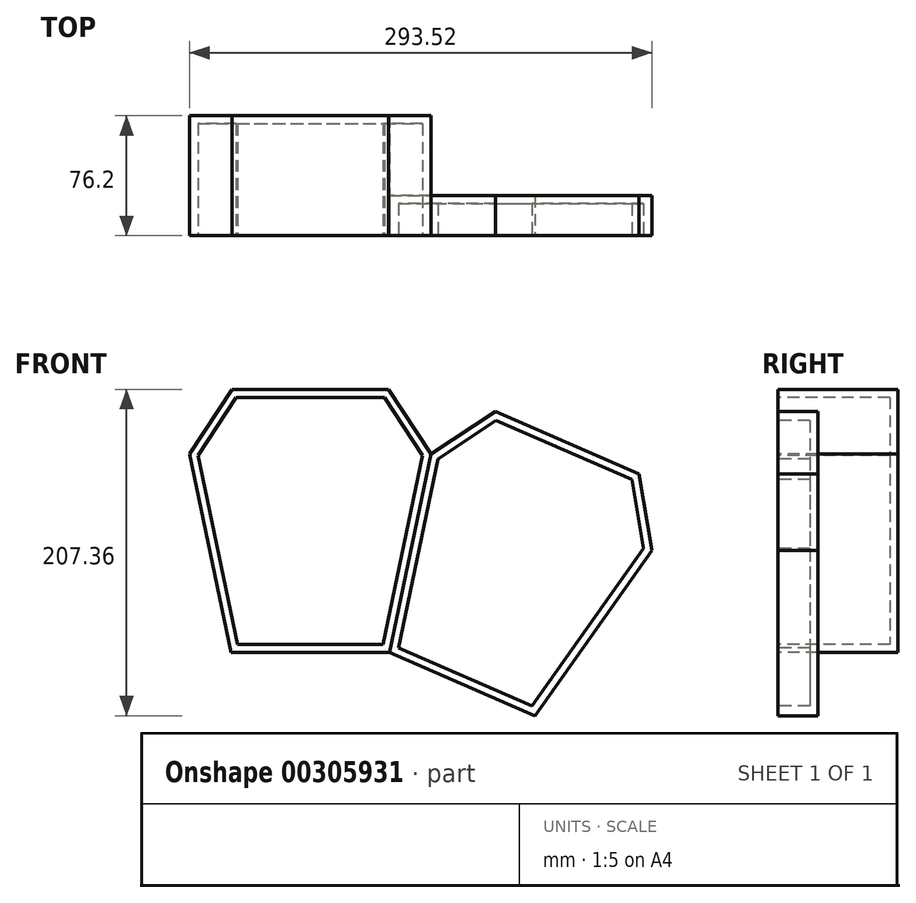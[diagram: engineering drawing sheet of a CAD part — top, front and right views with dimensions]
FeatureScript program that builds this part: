
annotation { "Feature Type Name" : "Feature", "Feature Type Description" : "" }
export const myFeature = defineFeature(function(context is Context, id is Id, definition is map)
    precondition{}
    {
        {
            var Q0;
            Q0=qCreatedBy(makeId("Front.planeOp"),FACE);
            var sketch = newSketch(context, id + "F0", { "sketchPlane" : qUnion([Q0])});
            skLineSegment(sketch, "E0", {"start": v(0, 0) * mm, "end": v(49.8, 0) * mm});
            skLineSegment(sketch, "E1", {"start": v(49.8, 0) * mm, "end": v(76.56, -41.16) * mm});
            skLineSegment(sketch, "E2", {"start": v(76.56, -41.16) * mm, "end": v(50.32, -167.2) * mm});
            skLineSegment(sketch, "E3", {"start": v(50.32, -167.2) * mm, "end": v(0, -167.2) * mm});
            skLineSegment(sketch, "E4.MirrorCS", {"start": v(0, 0) * mm, "end": v(-49.8, 0) * mm});
            skLineSegment(sketch, "E5.MirrorCS", {"start": v(-49.8, 0) * mm, "end": v(-76.56, -41.16) * mm});
            skLineSegment(sketch, "E6.MirrorCS", {"start": v(-76.56, -41.16) * mm, "end": v(-50.32, -167.2) * mm});
            skLineSegment(sketch, "E7.MirrorCS", {"start": v(-50.32, -167.2) * mm, "end": v(0, -167.2) * mm});
            skLineSegment(sketch, "E8.MirrorCS", {"start": v(117.52, -14.1) * mm, "end": v(76.56, -41.16) * mm});
            skLineSegment(sketch, "E9.MirrorCS", {"start": v(163.18, -33.96) * mm, "end": v(117.52, -14.1) * mm});
            skLineSegment(sketch, "E10.MirrorCS", {"start": v(163.18, -33.96) * mm, "end": v(208.83, -53.82) * mm});
            skLineSegment(sketch, "E11.MirrorCS", {"start": v(208.83, -53.82) * mm, "end": v(216.96, -102.24) * mm});
            skLineSegment(sketch, "E12.MirrorCS", {"start": v(216.96, -102.24) * mm, "end": v(142.61, -207.36) * mm});
            skLineSegment(sketch, "E13.MirrorCS", {"start": v(50.32, -167.2) * mm, "end": v(96.47, -187.29) * mm});
            skLineSegment(sketch, "E14.MirrorCS", {"start": v(142.61, -207.36) * mm, "end": v(96.47, -187.29) * mm});
            skSolve(sketch);
        }
        {
            var Q0;
            Q0=makeQuery(id+"F0.imprint","IMPRINT",FACE,{"disambiguationData":[TD([[makeQuery(id+"F0.imprint","IMPRINT",EDGE,{"derivedFrom":sQuery(id+"F0.wireOp",EDGE,"E0")}),-1.0]])]});
            extrude(context, id + "F1", {"entities" : qUnion([Q0]), "oppositeDirection" : true, "depth" : 76.2 * mm});
        }
        {
            var Q0;
            Q0=makeQuery(id+"F0.imprint","IMPRINT",FACE,{"disambiguationData":[TD([[makeQuery(id+"F0.imprint","IMPRINT",EDGE,{"derivedFrom":sQuery(id+"F0.wireOp",EDGE,"E2")}),1.0]])]});
            extrude(context, id + "F2", {"entities" : qUnion([Q0]), "oppositeDirection" : true, "depth" : 25.4 * mm});
        }
        {
            var Q0;
            Q0=makeQuery(id+"F1.opExtrude","CAP_FACE",FACE,{"disambiguationData":[OSD([sQuery(id+"F0.wireOp",EDGE,"E0"),sQuery(id+"F0.wireOp",EDGE,"E1"),sQuery(id+"F0.wireOp",EDGE,"E2"),sQuery(id+"F0.wireOp",EDGE,"E3"),sQuery(id+"F0.wireOp",EDGE,"E4.MirrorCS"),sQuery(id+"F0.wireOp",EDGE,"E5.MirrorCS"),sQuery(id+"F0.wireOp",EDGE,"E6.MirrorCS"),sQuery(id+"F0.wireOp",EDGE,"E7.MirrorCS")])],"isStart":true});
            shell(context, id + "F3", {"entities" : qUnion([Q0]), "thickness" : 5.08 * mm});
        }
        {
            var Q0;
            Q0=makeQuery(id+"F2.opExtrude","CAP_FACE",FACE,{"disambiguationData":[OSD([sQuery(id+"F0.wireOp",EDGE,"E2"),sQuery(id+"F0.wireOp",EDGE,"E8.MirrorCS"),sQuery(id+"F0.wireOp",EDGE,"E9.MirrorCS"),sQuery(id+"F0.wireOp",EDGE,"E10.MirrorCS"),sQuery(id+"F0.wireOp",EDGE,"E11.MirrorCS"),sQuery(id+"F0.wireOp",EDGE,"E12.MirrorCS"),sQuery(id+"F0.wireOp",EDGE,"E13.MirrorCS"),sQuery(id+"F0.wireOp",EDGE,"E14.MirrorCS")])],"isStart":true});
            shell(context, id + "F4", {"entities" : qUnion([Q0]), "thickness" : 5.08 * mm});
        }
    });
